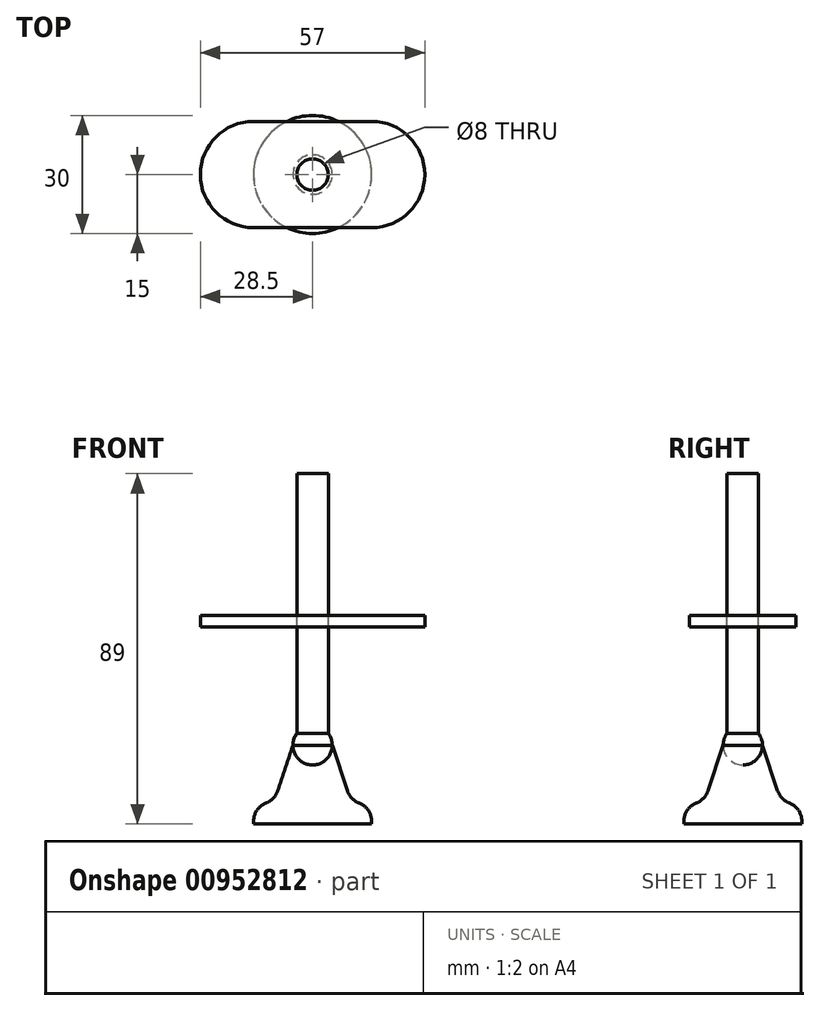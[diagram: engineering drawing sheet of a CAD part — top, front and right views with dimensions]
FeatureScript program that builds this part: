
annotation { "Feature Type Name" : "Feature", "Feature Type Description" : "" }
export const myFeature = defineFeature(function(context is Context, id is Id, definition is map)
    precondition{}
    {
        {
            var Q0;
            Q0=qCreatedBy(makeId("Front.planeOp"),FACE);
            var sketch = newSketch(context, id + "F0", { "sketchPlane" : qUnion([Q0])});
            skLineSegment(sketch, "E0", {"start": v(0, 0) * mm, "end": v(-15, 0) * mm});
            skLineSegment(sketch, "E1", {"start": v(0, 0) * mm, "end": v(0, 20) * mm, "construction": true});
            skArc(sketch, "E2", {"start": v(-5, 20) * mm, "mid": v(-3.54, 16.46) * mm, "end": v(0, 15) * mm});
            skPoint(sketch, "E3.visualSharp", {"position": v(-30, 20) * mm});
            skLineSegment(sketch, "E4", {"start": v(0, 15) * mm, "end": v(0, 0) * mm});
            skLineSegment(sketch, "E5", {"start": v(-15, 0) * mm, "end": v(-15, 0.67) * mm});
            skPoint(sketch, "E6.visualSharp", {"position": v(-13.44, 20) * mm});
            skLineSegment(sketch, "E7", {"start": v(-15, 5) * mm, "end": v(-13.6, 5) * mm});
            skLineSegment(sketch, "E8", {"start": v(-8.86, 8.42) * mm, "end": v(-5, 20) * mm});
            skPoint(sketch, "E9.visualSharp", {"position": v(-10, 5) * mm});
            skArc(sketch, "E9.filletArc", {"start": v(-11.8, 5.34) * mm, "mid": v(-9.99, 6.55) * mm, "end": v(-8.86, 8.42) * mm});
            skPoint(sketch, "E10.newPointB", {"position": v(-15, 5) * mm});
            skArc(sketch, "E10.filletArc", {"start": v(-11.8, 5.34) * mm, "mid": v(-14.12, 3.5) * mm, "end": v(-15, 0.67) * mm});
            skSolve(sketch);
        }
        {
            var Q0;
            Q0=makeQuery(id+"F0.imprint","IMPRINT",FACE,{"disambiguationData":[TD([[makeQuery(id+"F0.imprint","IMPRINT",EDGE,{"derivedFrom":sQuery(id+"F0.wireOp",EDGE,"E0")}),-1.0]])]});
            var Q1;
            Q1=sQuery(id+"F0.wireOp",EDGE,"E1");
            revolve(context, id + "F1", {"surfaceOperationType" : NewSurfaceOperationType.NEW, "entities" : qUnion([Q0]), "axis" : qUnion([Q1]), "revolveType" : RevolveType.FULL});
        }
        {
            var Q0;
            Q0=qCreatedBy(makeId("Front.planeOp"),FACE);
            var sketch = newSketch(context, id + "F2", { "sketchPlane" : qUnion([Q0])});
            skArc(sketch, "E11.0", {"start": v(-5, 20) * mm, "mid": v(-3.54, 16.46) * mm, "end": v(0, 15) * mm, "construction": true});
            skArc(sketch, "E12", {"start": v(-4, 23) * mm, "mid": v(-4.47, 17.76) * mm, "end": v(0, 15) * mm});
            skLineSegment(sketch, "E13.top", {"start": v(0, 89) * mm, "end": v(-4, 89) * mm});
            skLineSegment(sketch, "E13.left", {"start": v(0, 25) * mm, "end": v(0, 89) * mm});
            skLineSegment(sketch, "E13.right", {"start": v(-4, 23) * mm, "end": v(-4, 89) * mm});
            skLineSegment(sketch, "E14", {"start": v(0, 25) * mm, "end": v(0, 15) * mm});
            skSolve(sketch);
        }
        {
            var Q0;
            Q0=makeQuery(id+"F2.imprint","IMPRINT",FACE,{"disambiguationData":[TD([[makeQuery(id+"F2.imprint","IMPRINT",EDGE,{"derivedFrom":sQuery(id+"F2.wireOp",EDGE,"E12")}),1.0]])]});
            var Q1;
            Q1=sQuery(id+"F2.wireOp",EDGE,"E14");
            revolve(context, id + "F3", {"surfaceOperationType" : NewSurfaceOperationType.NEW, "entities" : qUnion([Q0]), "axis" : qUnion([Q1]), "revolveType" : RevolveType.FULL});
        }
        {
            var Q0;
            Q0=qCreatedBy(makeId("Top.planeOp"),FACE);
            cPlane(context, id + "F4", {"entities" : qUnion([Q0]), "cplaneType" : CPlaneType.OFFSET, "offset" : 50 * mm, "width" : 150 * mm, "height" : 150 * mm});
        }
        {
            var Q0;
            Q0=qCreatedBy(id+"F4.planeOp",FACE);
            var sketch = newSketch(context, id + "F5", { "sketchPlane" : qUnion([Q0])});
            skLineSegment(sketch, "E15.bottom", {"start": v(-15, 13.5) * mm, "end": v(15, 13.5) * mm});
            skLineSegment(sketch, "E15.top", {"start": v(-15, -13.5) * mm, "end": v(15, -13.5) * mm});
            skLineSegment(sketch, "E15.left", {"start": v(-28.5, 0) * mm, "end": v(-28.5, 0) * mm});
            skLineSegment(sketch, "E15.right", {"start": v(28.5, 0) * mm, "end": v(28.5, 0) * mm});
            skPoint(sketch, "E15.middle", {"position": v(0, 0) * mm});
            skPoint(sketch, "E16.visualSharp", {"position": v(-28.5, 13.5) * mm});
            skArc(sketch, "E16.filletArc", {"start": v(-15, 13.5) * mm, "mid": v(-24.55, 9.55) * mm, "end": v(-28.5, 0) * mm});
            skPoint(sketch, "E17.visualSharp", {"position": v(-28.5, -13.5) * mm});
            skArc(sketch, "E17.filletArc", {"start": v(-28.5, 0) * mm, "mid": v(-24.55, -9.55) * mm, "end": v(-15, -13.5) * mm});
            skPoint(sketch, "E18.visualSharp", {"position": v(28.5, -13.5) * mm});
            skArc(sketch, "E18.filletArc", {"start": v(15, -13.5) * mm, "mid": v(24.55, -9.55) * mm, "end": v(28.5, 0) * mm});
            skPoint(sketch, "E19.visualSharp", {"position": v(28.5, 13.5) * mm});
            skArc(sketch, "E19.filletArc", {"start": v(28.5, 0) * mm, "mid": v(24.55, 9.55) * mm, "end": v(15, 13.5) * mm});
            skCircle(sketch, "E20", {"center": v(0, 0) * mm, "radius": 4 * mm});
            skSolve(sketch);
        }
        {
            var Q0;
            Q0 = qSketchRegion(id + "F5", true);
            extrude(context, id + "F6", {"entities" : qUnion([Q0]), "depth" : 3 * mm, "offsetDistance" : 25 * mm});
        }
    });
